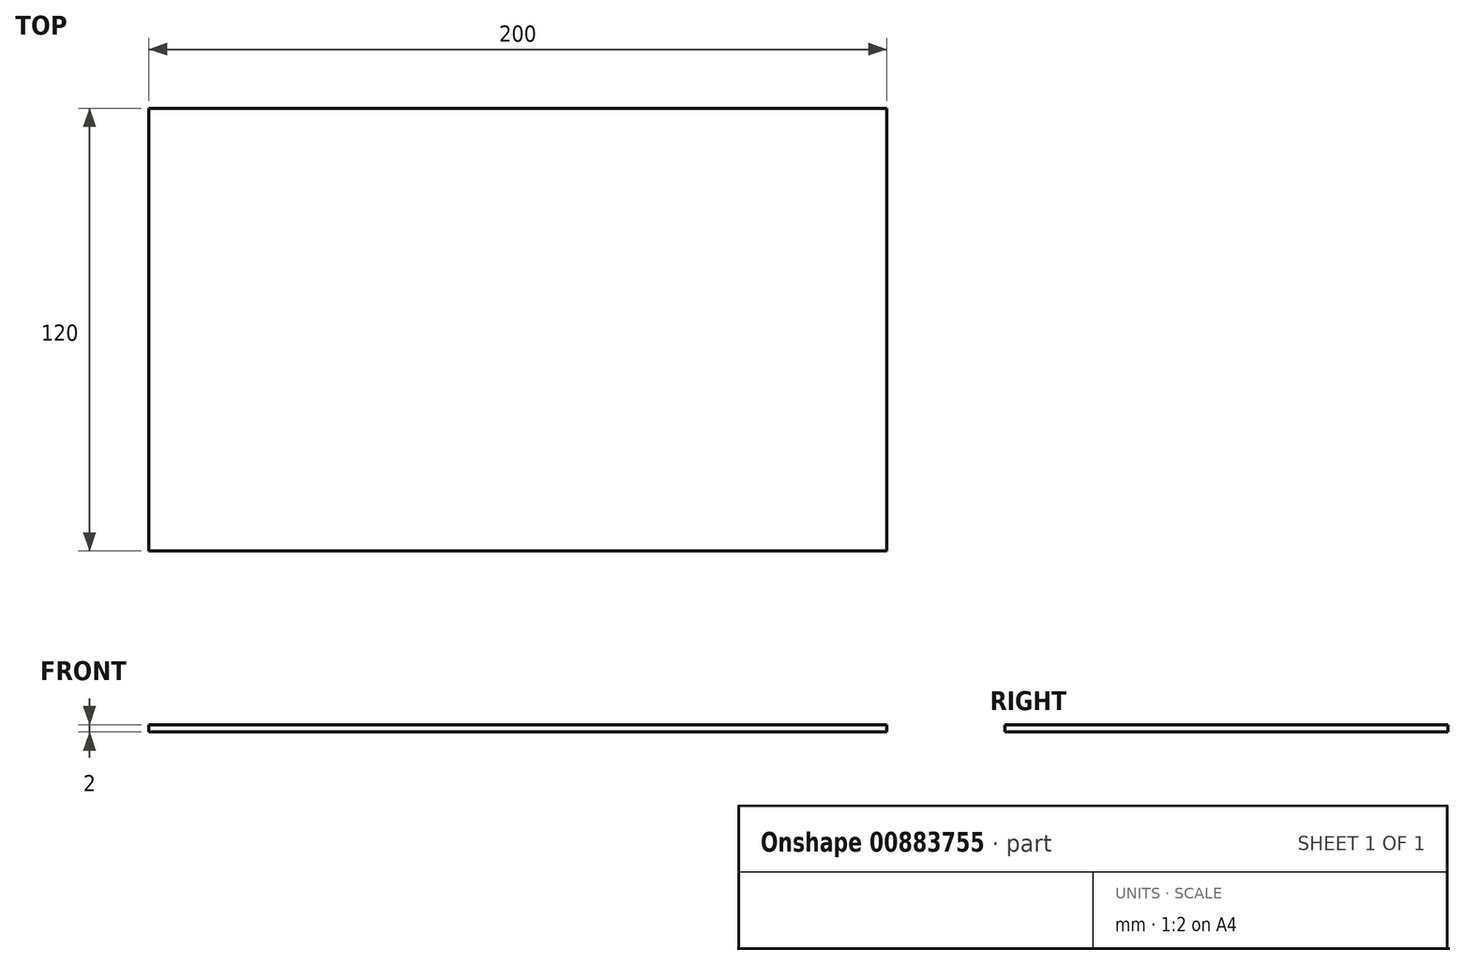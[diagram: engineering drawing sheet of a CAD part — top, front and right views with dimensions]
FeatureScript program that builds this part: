
annotation { "Feature Type Name" : "Feature", "Feature Type Description" : "" }
export const myFeature = defineFeature(function(context is Context, id is Id, definition is map)
    precondition{}
    {
        {
            var Q0;
            Q0=qCreatedBy(makeId("Top.planeOp"),FACE);
            var sketch = newSketch(context, id + "F0", { "sketchPlane" : qUnion([Q0])});
            skLineSegment(sketch, "E0.bottom", {"start": v(-2.8, -69.64) * mm, "end": v(-202.8, -69.64) * mm});
            skLineSegment(sketch, "E0.top", {"start": v(-2.8, 50.36) * mm, "end": v(-202.8, 50.36) * mm});
            skLineSegment(sketch, "E0.left", {"start": v(-2.8, -69.64) * mm, "end": v(-2.8, 50.36) * mm});
            skLineSegment(sketch, "E0.right", {"start": v(-202.8, -69.64) * mm, "end": v(-202.8, 50.36) * mm});
            skPoint(sketch, "E0.middle", {"position": v(-102.8, -9.64) * mm});
            skSolve(sketch);
        }
        {
            var Q0;
            Q0 = qSketchRegion(id + "F0", true);
            extrude(context, id + "F1", {"entities" : qUnion([Q0]), "depth" : 2 * mm, "offsetDistance" : 25 * mm});
        }
    });
